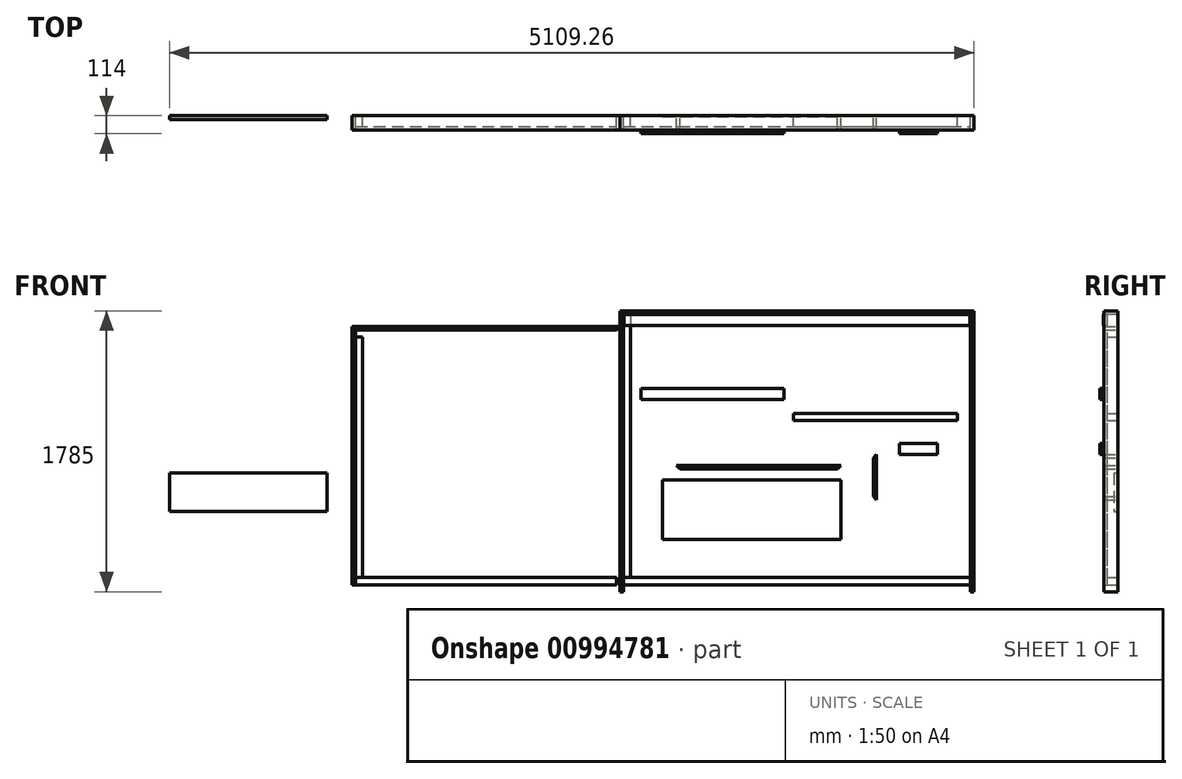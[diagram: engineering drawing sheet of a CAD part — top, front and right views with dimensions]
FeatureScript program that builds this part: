
annotation { "Feature Type Name" : "Feature", "Feature Type Description" : "" }
export const myFeature = defineFeature(function(context is Context, id is Id, definition is map)
    precondition{}
    {
        {
            var Q0;
            Q0=qCreatedBy(makeId("Front.planeOp"),FACE);
            var sketch = newSketch(context, id + "F0", { "sketchPlane" : qUnion([Q0])});
            skLineSegment(sketch, "E0", {"start": v(0, 0) * mm, "end": v(2250, 0) * mm});
            skLineSegment(sketch, "E1", {"start": v(2250, 0) * mm, "end": v(2250, 1740) * mm});
            skLineSegment(sketch, "E2", {"start": v(2250, 1740) * mm, "end": v(0, 1740) * mm});
            skLineSegment(sketch, "E3", {"start": v(0, 1740) * mm, "end": v(0, 1640) * mm});
            skLineSegment(sketch, "E4", {"start": v(0, 1640) * mm, "end": v(-1700, 1640) * mm});
            skLineSegment(sketch, "E5", {"start": v(-1700, 1640) * mm, "end": v(-1700, 0) * mm});
            skLineSegment(sketch, "E6", {"start": v(-1700, 0) * mm, "end": v(0, 0) * mm});
            skSolve(sketch);
        }
        {
            var Q0;
            Q0=makeQuery(id+"F0.imprint","IMPRINT",FACE,{"disambiguationData":[TD([[makeQuery(id+"F0.imprint","IMPRINT",EDGE,{"derivedFrom":sQuery(id+"F0.wireOp",EDGE,"E0")}),1.0]])]});
            var sketch = newSketch(context, id + "F1", { "sketchPlane" : qUnion([Q0])});
            skLineSegment(sketch, "E7.bottom", {"start": v(22, 45) * mm, "end": v(2228, 45) * mm});
            skLineSegment(sketch, "E7.top", {"start": v(22, 0) * mm, "end": v(2228, 0) * mm});
            skLineSegment(sketch, "E7.left", {"start": v(22, 45) * mm, "end": v(22, 0) * mm});
            skLineSegment(sketch, "E7.right", {"start": v(2228, 45) * mm, "end": v(2228, 0) * mm});
            skSolve(sketch);
        }
        {
            var Q0;
            Q0 = qSketchRegion(id + "F1", true);
            extrude(context, id + "F2", {"entities" : qUnion([Q0]), "depth" : 70 * mm, "offsetDistance" : 25 * mm});
        }
        {
            var Q0;
            Q0=makeQuery(id+"F0.imprint","IMPRINT",FACE,{"disambiguationData":[TD([[makeQuery(id+"F0.imprint","IMPRINT",EDGE,{"derivedFrom":sQuery(id+"F0.wireOp",EDGE,"E0")}),1.0]])]});
            var sketch = newSketch(context, id + "F3", { "sketchPlane" : qUnion([Q0])});
            skLineSegment(sketch, "E8.bottom", {"start": v(22, 1718) * mm, "end": v(67, 1718) * mm});
            skLineSegment(sketch, "E8.top", {"start": v(22, 45) * mm, "end": v(67, 45) * mm});
            skLineSegment(sketch, "E8.left", {"start": v(22, 1718) * mm, "end": v(22, 45) * mm});
            skLineSegment(sketch, "E8.right", {"start": v(67, 1718) * mm, "end": v(67, 45) * mm});
            skSolve(sketch);
        }
        {
            var Q0;
            Q0 = qSketchRegion(id + "F3", true);
            extrude(context, id + "F4", {"entities" : qUnion([Q0]), "depth" : 70 * mm, "offsetDistance" : 25 * mm});
        }
        {
            var Q0;
            Q0=makeQuery(id+"F0.imprint","IMPRINT",FACE,{"disambiguationData":[TD([[makeQuery(id+"F0.imprint","IMPRINT",EDGE,{"derivedFrom":sQuery(id+"F0.wireOp",EDGE,"E0")}),1.0]])]});
            var sketch = newSketch(context, id + "F5", { "sketchPlane" : qUnion([Q0])});
            skLineSegment(sketch, "E9", {"start": v(0, 1740) * mm, "end": v(2250, 1740) * mm});
            skLineSegment(sketch, "E10", {"start": v(22, 1718) * mm, "end": v(2228, 1718) * mm});
            skLineSegment(sketch, "E11", {"start": v(2250, 1740) * mm, "end": v(2228, 1718) * mm});
            skLineSegment(sketch, "E12", {"start": v(22, 1718) * mm, "end": v(0, 1740) * mm});
            skSolve(sketch);
        }
        {
            var Q0;
            Q0 = qSketchRegion(id + "F5", true);
            extrude(context, id + "F6", {"entities" : qUnion([Q0]), "depth" : 90 * mm, "offsetDistance" : 25 * mm});
        }
        {
            var Q0;
            Q0=makeQuery(id+"F0.imprint","IMPRINT",FACE,{"disambiguationData":[TD([[makeQuery(id+"F0.imprint","IMPRINT",EDGE,{"derivedFrom":sQuery(id+"F0.wireOp",EDGE,"E0")}),1.0]])]});
            var sketch = newSketch(context, id + "F7", { "sketchPlane" : qUnion([Q0])});
            skLineSegment(sketch, "E13", {"start": v(2250, 1740) * mm, "end": v(2250, -45) * mm});
            skLineSegment(sketch, "E14", {"start": v(2250, -45) * mm, "end": v(2228, -45) * mm});
            skLineSegment(sketch, "E15", {"start": v(2228, -45) * mm, "end": v(2228, 1718) * mm});
            skLineSegment(sketch, "E16", {"start": v(2228, 1718) * mm, "end": v(2250, 1740) * mm});
            skSolve(sketch);
        }
        {
            var Q0;
            Q0 = qSketchRegion(id + "F7", true);
            extrude(context, id + "F8", {"entities" : qUnion([Q0]), "depth" : 90 * mm, "offsetDistance" : 25 * mm});
        }
        {
            var Q0;
            Q0=makeQuery(id+"F0.imprint","IMPRINT",FACE,{"disambiguationData":[TD([[makeQuery(id+"F0.imprint","IMPRINT",EDGE,{"derivedFrom":sQuery(id+"F0.wireOp",EDGE,"E0")}),1.0]])]});
            var sketch = newSketch(context, id + "F9", { "sketchPlane" : qUnion([Q0])});
            skLineSegment(sketch, "E17", {"start": v(0, 1740) * mm, "end": v(0, -45) * mm});
            skLineSegment(sketch, "E18", {"start": v(0, -45) * mm, "end": v(22, -45) * mm});
            skLineSegment(sketch, "E19", {"start": v(22, -45) * mm, "end": v(22, 1718) * mm});
            skLineSegment(sketch, "E20", {"start": v(22, 1718) * mm, "end": v(0, 1740) * mm});
            skSolve(sketch);
        }
        {
            var Q0;
            Q0 = qSketchRegion(id + "F9", true);
            extrude(context, id + "F10", {"entities" : qUnion([Q0]), "depth" : 90 * mm, "offsetDistance" : 25 * mm});
        }
        {
            var Q0;
            Q0=makeQuery(id+"F2.opExtrude","CAP_FACE",FACE,{"disambiguationData":[OSD([sQuery(id+"F1.wireOp",EDGE,"E7.bottom"),sQuery(id+"F1.wireOp",EDGE,"E7.top"),sQuery(id+"F1.wireOp",EDGE,"E7.left"),sQuery(id+"F1.wireOp",EDGE,"E7.right")])],"isStart":false});
            var sketch = newSketch(context, id + "F11", { "sketchPlane" : qUnion([Q0])});
            skLineSegment(sketch, "E21.bottom", {"start": v(25, 1645) * mm, "end": v(2225, 1645) * mm});
            skLineSegment(sketch, "E21.top", {"start": v(25, 1715) * mm, "end": v(2225, 1715) * mm});
            skLineSegment(sketch, "E21.left", {"start": v(25, 1715) * mm, "end": v(25, 1645) * mm});
            skLineSegment(sketch, "E21.right", {"start": v(2225, 1715) * mm, "end": v(2225, 1645) * mm});
            skSolve(sketch);
        }
        {
            var Q0;
            Q0 = qSketchRegion(id + "F11", true);
            extrude(context, id + "F12", {"entities" : qUnion([Q0]), "depth" : 22 * mm, "offsetDistance" : 25 * mm});
        }
        {
            var Q0;
            Q0=makeQuery(id+"F0.imprint","IMPRINT",FACE,{"disambiguationData":[TD([[makeQuery(id+"F0.imprint","IMPRINT",EDGE,{"derivedFrom":sQuery(id+"F0.wireOp",EDGE,"E0")}),1.0]])]});
            var sketch = newSketch(context, id + "F13", { "sketchPlane" : qUnion([Q0])});
            skLineSegment(sketch, "E22.bottom", {"start": v(1101.65, 1087.37) * mm, "end": v(2145.65, 1087.37) * mm});
            skLineSegment(sketch, "E22.top", {"start": v(1101.65, 1042.37) * mm, "end": v(2145.65, 1042.37) * mm});
            skLineSegment(sketch, "E22.left", {"start": v(1101.65, 1087.37) * mm, "end": v(1101.65, 1042.37) * mm});
            skLineSegment(sketch, "E22.right", {"start": v(2145.65, 1087.37) * mm, "end": v(2145.65, 1042.37) * mm});
            skSolve(sketch);
        }
        {
            var Q0;
            Q0 = qSketchRegion(id + "F13", true);
            extrude(context, id + "F14", {"entities" : qUnion([Q0]), "depth" : 70 * mm, "offsetDistance" : 25 * mm});
        }
        {
            var Q0;
            Q0=makeQuery(id+"F12.opExtrude","CAP_FACE",FACE,{"disambiguationData":[OSD([sQuery(id+"F11.wireOp",EDGE,"E21.bottom"),sQuery(id+"F11.wireOp",EDGE,"E21.top"),sQuery(id+"F11.wireOp",EDGE,"E21.left"),sQuery(id+"F11.wireOp",EDGE,"E21.right")])],"isStart":false});
            var sketch = newSketch(context, id + "F15", { "sketchPlane" : qUnion([Q0])});
            skLineSegment(sketch, "E23.bottom", {"start": v(135.69, 1247.8) * mm, "end": v(1041.69, 1247.8) * mm});
            skLineSegment(sketch, "E23.top", {"start": v(135.69, 1177.8) * mm, "end": v(1041.69, 1177.8) * mm});
            skLineSegment(sketch, "E23.left", {"start": v(135.69, 1247.8) * mm, "end": v(135.69, 1177.8) * mm});
            skLineSegment(sketch, "E23.right", {"start": v(1041.69, 1247.8) * mm, "end": v(1041.69, 1177.8) * mm});
            skSolve(sketch);
        }
        {
            var Q0;
            Q0 = qSketchRegion(id + "F15", true);
            extrude(context, id + "F16", {"entities" : qUnion([Q0]), "depth" : 22 * mm, "offsetDistance" : 25 * mm});
        }
        {
            var Q0;
            Q0=makeQuery(id+"F12.opExtrude","CAP_FACE",FACE,{"disambiguationData":[OSD([sQuery(id+"F11.wireOp",EDGE,"E21.bottom"),sQuery(id+"F11.wireOp",EDGE,"E21.top"),sQuery(id+"F11.wireOp",EDGE,"E21.left"),sQuery(id+"F11.wireOp",EDGE,"E21.right")])],"isStart":false});
            var sketch = newSketch(context, id + "F17", { "sketchPlane" : qUnion([Q0])});
            skLineSegment(sketch, "E24.bottom", {"start": v(1774.65, 898.53) * mm, "end": v(2018.65, 898.53) * mm});
            skLineSegment(sketch, "E24.top", {"start": v(1774.65, 828.53) * mm, "end": v(2018.65, 828.53) * mm});
            skLineSegment(sketch, "E24.left", {"start": v(1774.65, 898.53) * mm, "end": v(1774.65, 828.53) * mm});
            skLineSegment(sketch, "E24.right", {"start": v(2018.65, 898.53) * mm, "end": v(2018.65, 828.53) * mm});
            skSolve(sketch);
        }
        {
            var Q0;
            Q0 = qSketchRegion(id + "F17", true);
            extrude(context, id + "F18", {"entities" : qUnion([Q0]), "depth" : 22 * mm, "offsetDistance" : 25 * mm});
        }
        {
            var Q0;
            Q0=makeQuery(id+"F0.imprint","IMPRINT",FACE,{"disambiguationData":[TD([[makeQuery(id+"F0.imprint","IMPRINT",EDGE,{"derivedFrom":sQuery(id+"F0.wireOp",EDGE,"E0")}),1.0]])]});
            var sketch = newSketch(context, id + "F19", { "sketchPlane" : qUnion([Q0])});
            skLineSegment(sketch, "E25", {"start": v(1631.49, 826.34) * mm, "end": v(1631.49, 537.34) * mm});
            skLineSegment(sketch, "E26", {"start": v(1631.49, 537.34) * mm, "end": v(1609.49, 559.34) * mm});
            skLineSegment(sketch, "E27", {"start": v(1609.49, 559.34) * mm, "end": v(1609.49, 804.34) * mm});
            skLineSegment(sketch, "E28", {"start": v(1609.49, 804.34) * mm, "end": v(1631.49, 826.34) * mm});
            skSolve(sketch);
        }
        {
            var Q0;
            Q0 = qSketchRegion(id + "F19", true);
            extrude(context, id + "F20", {"entities" : qUnion([Q0]), "depth" : 90 * mm, "offsetDistance" : 25 * mm});
        }
        {
            var Q0;
            Q0=makeQuery(id+"F0.imprint","IMPRINT",FACE,{"disambiguationData":[TD([[makeQuery(id+"F0.imprint","IMPRINT",EDGE,{"derivedFrom":sQuery(id+"F0.wireOp",EDGE,"E0")}),1.0]])]});
            var sketch = newSketch(context, id + "F21", { "sketchPlane" : qUnion([Q0])});
            skLineSegment(sketch, "E29", {"start": v(361.28, 757.17) * mm, "end": v(1405.28, 757.17) * mm});
            skLineSegment(sketch, "E30", {"start": v(1405.28, 757.17) * mm, "end": v(1383.28, 735.17) * mm});
            skLineSegment(sketch, "E31", {"start": v(1383.28, 735.17) * mm, "end": v(383.28, 735.17) * mm});
            skLineSegment(sketch, "E32", {"start": v(383.28, 735.17) * mm, "end": v(361.28, 757.17) * mm});
            skSolve(sketch);
        }
        {
            var Q0;
            Q0 = qSketchRegion(id + "F21", true);
            extrude(context, id + "F22", {"entities" : qUnion([Q0]), "depth" : 90 * mm, "offsetDistance" : 25 * mm});
        }
        {
            var Q0;
            Q0=makeQuery(id+"F0.imprint","IMPRINT",FACE,{"disambiguationData":[TD([[makeQuery(id+"F0.imprint","IMPRINT",EDGE,{"derivedFrom":sQuery(id+"F0.wireOp",EDGE,"E0")}),1.0]])]});
            var sketch = newSketch(context, id + "F23", { "sketchPlane" : qUnion([Q0])});
            skLineSegment(sketch, "E33.bottom", {"start": v(270.99, 666.82) * mm, "end": v(1404.99, 666.82) * mm});
            skLineSegment(sketch, "E33.top", {"start": v(270.99, 287.82) * mm, "end": v(1404.99, 287.82) * mm});
            skLineSegment(sketch, "E33.left", {"start": v(270.99, 666.82) * mm, "end": v(270.99, 287.82) * mm});
            skLineSegment(sketch, "E33.right", {"start": v(1404.99, 666.82) * mm, "end": v(1404.99, 287.82) * mm});
            skSolve(sketch);
        }
        {
            var Q0;
            Q0 = qSketchRegion(id + "F23", true);
            extrude(context, id + "F24", {"entities" : qUnion([Q0]), "depth" : 5 * mm, "offsetDistance" : 25 * mm});
        }
        {
            var Q0;
            Q0=makeQuery(id+"F0.imprint","IMPRINT",FACE,{"disambiguationData":[TD([[makeQuery(id+"F0.imprint","IMPRINT",EDGE,{"derivedFrom":sQuery(id+"F0.wireOp",EDGE,"E0")}),1.0]])]});
            var sketch = newSketch(context, id + "F25", { "sketchPlane" : qUnion([Q0])});
            skLineSegment(sketch, "E34.bottom", {"start": v(-2859.26, 709.97) * mm, "end": v(-1859.26, 709.97) * mm});
            skLineSegment(sketch, "E34.top", {"start": v(-2859.26, 464.97) * mm, "end": v(-1859.26, 464.97) * mm});
            skLineSegment(sketch, "E34.left", {"start": v(-2859.26, 709.97) * mm, "end": v(-2859.26, 464.97) * mm});
            skLineSegment(sketch, "E34.right", {"start": v(-1859.26, 709.97) * mm, "end": v(-1859.26, 464.97) * mm});
            skSolve(sketch);
        }
        {
            var Q0;
            Q0 = qSketchRegion(id + "F25", true);
            extrude(context, id + "F26", {"entities" : qUnion([Q0]), "depth" : 25 * mm, "offsetDistance" : 25 * mm});
        }
        {
            var Q0;
            Q0=makeQuery(id+"F0.imprint","IMPRINT",FACE,{"disambiguationData":[TD([[makeQuery(id+"F0.imprint","IMPRINT",EDGE,{"derivedFrom":sQuery(id+"F0.wireOp",EDGE,"E0")}),1.0]])]});
            var sketch = newSketch(context, id + "F27", { "sketchPlane" : qUnion([Q0])});
            skLineSegment(sketch, "E35.bottom", {"start": v(-1678, 0) * mm, "end": v(-22, 0) * mm});
            skLineSegment(sketch, "E35.top", {"start": v(-1678, 45) * mm, "end": v(-22, 45) * mm});
            skLineSegment(sketch, "E35.left", {"start": v(-1678, 0) * mm, "end": v(-1678, 45) * mm});
            skLineSegment(sketch, "E35.right", {"start": v(-22, 0) * mm, "end": v(-22, 45) * mm});
            skSolve(sketch);
        }
        {
            var Q0;
            Q0 = qSketchRegion(id + "F27", true);
            extrude(context, id + "F28", {"entities" : qUnion([Q0]), "depth" : 70 * mm, "offsetDistance" : 25 * mm});
        }
        {
            var Q0;
            Q0=makeQuery(id+"F0.imprint","IMPRINT",FACE,{"disambiguationData":[TD([[makeQuery(id+"F0.imprint","IMPRINT",EDGE,{"derivedFrom":sQuery(id+"F0.wireOp",EDGE,"E0")}),1.0]])]});
            var sketch = newSketch(context, id + "F29", { "sketchPlane" : qUnion([Q0])});
            skLineSegment(sketch, "E36.bottom", {"start": v(-1678, 1573) * mm, "end": v(-1633, 1573) * mm});
            skLineSegment(sketch, "E36.top", {"start": v(-1678, 45) * mm, "end": v(-1633, 45) * mm});
            skLineSegment(sketch, "E36.left", {"start": v(-1678, 1573) * mm, "end": v(-1678, 45) * mm});
            skLineSegment(sketch, "E36.right", {"start": v(-1633, 1573) * mm, "end": v(-1633, 45) * mm});
            skSolve(sketch);
        }
        {
            var Q0;
            Q0 = qSketchRegion(id + "F29", true);
            extrude(context, id + "F30", {"entities" : qUnion([Q0]), "depth" : 70 * mm, "offsetDistance" : 25 * mm});
        }
        {
            var Q0;
            Q0=makeQuery(id+"F0.imprint","IMPRINT",FACE,{"disambiguationData":[TD([[makeQuery(id+"F0.imprint","IMPRINT",EDGE,{"derivedFrom":sQuery(id+"F0.wireOp",EDGE,"E0")}),1.0]])]});
            var sketch = newSketch(context, id + "F31", { "sketchPlane" : qUnion([Q0])});
            skLineSegment(sketch, "E37", {"start": v(-1700, 1640) * mm, "end": v(-1700, 0) * mm});
            skLineSegment(sketch, "E38", {"start": v(-1700, 0) * mm, "end": v(-1678, 0) * mm});
            skLineSegment(sketch, "E39", {"start": v(-1678, 0) * mm, "end": v(-1678, 1618) * mm});
            skLineSegment(sketch, "E40", {"start": v(-1678, 1618) * mm, "end": v(-1700, 1640) * mm});
            skSolve(sketch);
        }
        {
            var Q0;
            Q0 = qSketchRegion(id + "F31", true);
            extrude(context, id + "F32", {"entities" : qUnion([Q0]), "depth" : 90 * mm, "offsetDistance" : 25 * mm});
        }
        {
            var Q0;
            Q0=makeQuery(id+"F0.imprint","IMPRINT",FACE,{"disambiguationData":[TD([[makeQuery(id+"F0.imprint","IMPRINT",EDGE,{"derivedFrom":sQuery(id+"F0.wireOp",EDGE,"E0")}),1.0]])]});
            var sketch = newSketch(context, id + "F33", { "sketchPlane" : qUnion([Q0])});
            skLineSegment(sketch, "E41", {"start": v(-1700, 1640) * mm, "end": v(0, 1640) * mm});
            skLineSegment(sketch, "E42", {"start": v(0, 1640) * mm, "end": v(-22, 1618) * mm});
            skLineSegment(sketch, "E43", {"start": v(-22, 1618) * mm, "end": v(-1678, 1618) * mm});
            skLineSegment(sketch, "E44", {"start": v(-1678, 1618) * mm, "end": v(-1700, 1640) * mm});
            skSolve(sketch);
        }
        {
            var Q0;
            Q0 = qSketchRegion(id + "F33", true);
            extrude(context, id + "F34", {"entities" : qUnion([Q0]), "depth" : 90 * mm, "offsetDistance" : 25 * mm});
        }
    });
